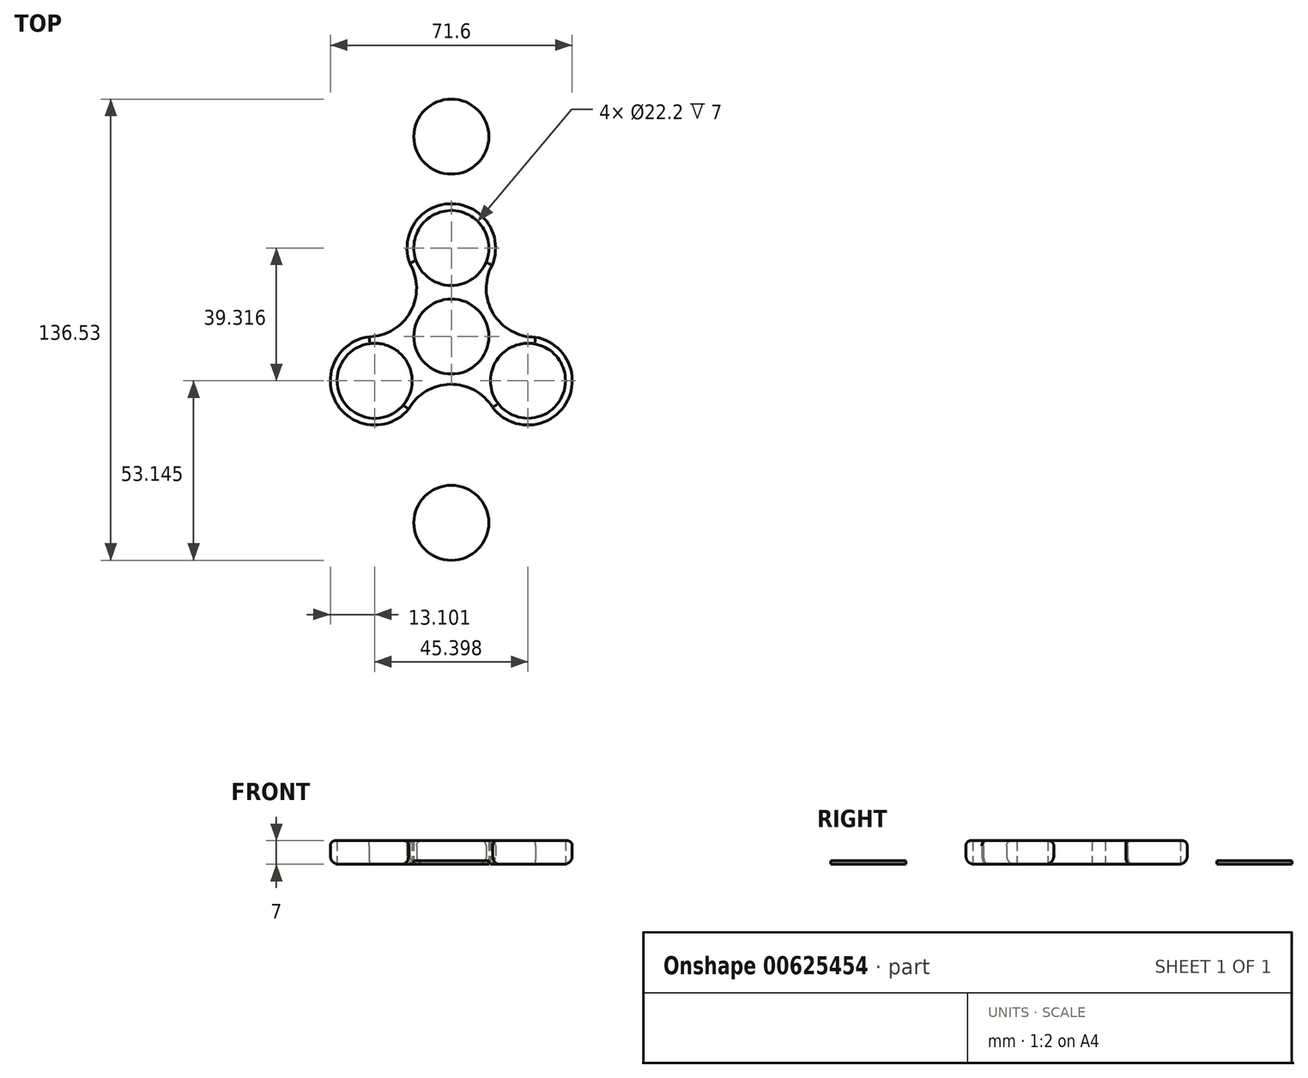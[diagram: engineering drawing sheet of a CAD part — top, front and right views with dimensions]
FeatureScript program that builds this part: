
annotation { "Feature Type Name" : "Feature", "Feature Type Description" : "" }
export const myFeature = defineFeature(function(context is Context, id is Id, definition is map)
    precondition{}
    {
        {
            var Q0;
            Q0=qCreatedBy(makeId("Top.planeOp"),FACE);
            var sketch = newSketch(context, id + "F0", { "sketchPlane" : qUnion([Q0])});
            skCircle(sketch, "E0", {"center": v(0, 0) * mm, "radius": 11.1 * mm});
            skCircle(sketch, "E1", {"center": v(0, 26.21) * mm, "radius": 11.1 * mm});
            skCircle(sketch, "E2.1.0", {"center": v(-22.7, -13.1) * mm, "radius": 11.1 * mm});
            skCircle(sketch, "E2.2.0", {"center": v(22.7, -13.1) * mm, "radius": 11.1 * mm});
            skArc(sketch, "E2.2.1", {"start": v(12.11, -20.82) * mm, "mid": v(33.83, -20.01) * mm, "end": v(24.9, -0.2) * mm});
            skArc(sketch, "E3", {"start": v(-24.31, -0.1) * mm, "mid": v(-34.06, -19.62) * mm, "end": v(-12.3, -21.06) * mm});
            skArc(sketch, "E4", {"start": v(-24.09, -0.08) * mm, "mid": v(-24.2, -0.1) * mm, "end": v(-24.31, -0.1) * mm});
            skArc(sketch, "E5", {"start": v(11.98, 20.9) * mm, "mid": v(12.02, 21) * mm, "end": v(12.06, 21.1) * mm});
            skArc(sketch, "E6", {"start": v(12.06, 21.1) * mm, "mid": v(0.2, 39.3) * mm, "end": v(-12.21, 21.47) * mm});
            skArc(sketch, "E7", {"start": v(12.06, 21.1) * mm, "mid": v(12.41, 6.8) * mm, "end": v(24.9, -0.2) * mm});
            skArc(sketch, "E8.1.0", {"start": v(-24.31, -0.1) * mm, "mid": v(-12.1, 7.35) * mm, "end": v(-12.29, 21.67) * mm});
            skArc(sketch, "E8.2.0", {"start": v(12.25, -21) * mm, "mid": v(-0.32, -14.15) * mm, "end": v(-12.62, -21.48) * mm});
            skPoint(sketch, "E9.start.orphan", {"position": v(0, 24.31) * mm});
            skSolve(sketch);
        }
        {
            var Q0;
            Q0=makeQuery(id+"F0.imprint","IMPRINT",FACE,{"disambiguationData":[TD([[makeQuery(id+"F0.imprint","IMPRINT",EDGE,{"derivedFrom":sQuery(id+"F0.wireOp",EDGE,"E0")}),-1.0]])]});
            extrude(context, id + "F1", {"entities" : qUnion([Q0]), "depth" : 7 * mm, "offsetDistance" : 25 * mm});
        }
        {
            var Q0;
            Q0=makeQuery(id+"F1.opExtrude","CAP_EDGE",EDGE,{"disambiguationData":[OSD([sQuery(id+"F0.wireOp",EDGE,"E8.2.0")])],"isStart":false});
            var Q1;
            Q1=makeQuery(id+"F1.opExtrude","CAP_EDGE",EDGE,{"disambiguationData":[OSD([sQuery(id+"F0.wireOp",EDGE,"E3")])],"isStart":false});
            var Q2;
            Q2=makeQuery(id+"F1.opExtrude","CAP_EDGE",EDGE,{"disambiguationData":[OSD([sQuery(id+"F0.wireOp",EDGE,"E8.1.0")])],"isStart":false});
            var Q3;
            Q3=makeQuery(id+"F1.opExtrude","CAP_EDGE",EDGE,{"disambiguationData":[OSD([sQuery(id+"F0.wireOp",EDGE,"E7")])],"isStart":false});
            var Q4;
            Q4=makeQuery(id+"F1.opExtrude","CAP_EDGE",EDGE,{"disambiguationData":[OSD([sQuery(id+"F0.wireOp",EDGE,"E6")])],"isStart":false});
            var Q5;
            Q5=makeQuery(id+"F1.opExtrude","CAP_EDGE",EDGE,{"disambiguationData":[OSD([sQuery(id+"F0.wireOp",EDGE,"E2.2.1")])],"isStart":false});
            fillet(context, id + "F2", {"entities" : qUnion([Q0, Q1, Q2, Q3, Q4, Q5]), "radius" : 1.5 * mm, "tangentPropagation" : true, "allowEdgeOverflow" : false});
        }
        {
            var Q0;
            Q0=makeQuery(id+"F1.opExtrude","CAP_EDGE",EDGE,{"disambiguationData":[OSD([sQuery(id+"F0.wireOp",EDGE,"E8.2.0")])],"isStart":true});
            var Q1;
            Q1=makeQuery(id+"F1.opExtrude","CAP_EDGE",EDGE,{"disambiguationData":[OSD([sQuery(id+"F0.wireOp",EDGE,"E3")])],"isStart":true});
            var Q2;
            Q2=makeQuery(id+"F1.opExtrude","CAP_EDGE",EDGE,{"disambiguationData":[OSD([sQuery(id+"F0.wireOp",EDGE,"E2.2.1")])],"isStart":true});
            var Q3;
            Q3=makeQuery(id+"F1.opExtrude","CAP_EDGE",EDGE,{"disambiguationData":[OSD([sQuery(id+"F0.wireOp",EDGE,"E7")])],"isStart":true});
            var Q4;
            Q4=makeQuery(id+"F1.opExtrude","CAP_EDGE",EDGE,{"disambiguationData":[OSD([sQuery(id+"F0.wireOp",EDGE,"E6")])],"isStart":true});
            var Q5;
            Q5=makeQuery(id+"F1.opExtrude","CAP_EDGE",EDGE,{"disambiguationData":[OSD([sQuery(id+"F0.wireOp",EDGE,"E8.1.0")])],"isStart":true});
            fillet(context, id + "F3", {"entities" : qUnion([Q0, Q1, Q2, Q3, Q4, Q5]), "radius" : 2.5 * mm, "tangentPropagation" : true, "allowEdgeOverflow" : false});
        }
        {
            var Q0;
            Q0=qCreatedBy(makeId("Top.planeOp"),FACE);
            var sketch = newSketch(context, id + "F4", { "sketchPlane" : qUnion([Q0])});
            skCircle(sketch, "E10", {"center": v(0, -55.15) * mm, "radius": 11.1 * mm});
            skCircle(sketch, "E11", {"center": v(0, 59.18) * mm, "radius": 11.1 * mm});
            skArc(sketch, "E12", {"start": v(-1.77, -50.53) * mm, "mid": v(-4.95, -55.24) * mm, "end": v(-1.6, -59.83) * mm});
            skArc(sketch, "E13", {"start": v(1.63, -59.82) * mm, "mid": v(4.95, -55.25) * mm, "end": v(1.83, -50.55) * mm});
            skArc(sketch, "E14", {"start": v(-2.36, 63.53) * mm, "mid": v(-4.95, 59) * mm, "end": v(-2.05, 54.68) * mm});
            skArc(sketch, "E15", {"start": v(2.1, 54.7) * mm, "mid": v(4.95, 59.2) * mm, "end": v(2.07, 63.68) * mm});
            skSolve(sketch);
        }
        {
            var Q0;
            Q0=makeQuery(id+"F4.imprint","IMPRINT",FACE,{"disambiguationData":[TD([[makeQuery(id+"F4.imprint","IMPRINT",EDGE,{"derivedFrom":sQuery(id+"F4.wireOp",EDGE,"E10")}),1.0]])]});
            extrude(context, id + "F5", {"entities" : qUnion([Q0]), "depth" : 1 * mm, "offsetDistance" : 25 * mm});
        }
        {
            var Q0;
            Q0=makeQuery(id+"F4.imprint","IMPRINT",FACE,{"disambiguationData":[TD([[makeQuery(id+"F4.imprint","IMPRINT",EDGE,{"derivedFrom":sQuery(id+"F4.wireOp",EDGE,"E11")}),1.0]])]});
            extrude(context, id + "F6", {"entities" : qUnion([Q0]), "depth" : 1 * mm, "offsetDistance" : 25 * mm});
        }
        {
            var Q0;
            Q0=sQuery(id+"F4.wireOp",EDGE,"E15");
            extrude(context, id + "F7", {"bodyType" : ToolBodyType.SURFACE, "surfaceEntities" : qUnion([Q0]), "depth" : 3 * mm, "offsetDistance" : 25 * mm});
        }
        {
            var Q0;
            Q0=sQuery(id+"F4.wireOp",EDGE,"E14");
            extrude(context, id + "F8", {"bodyType" : ToolBodyType.SURFACE, "surfaceEntities" : qUnion([Q0]), "depth" : 3 * mm, "offsetDistance" : 25 * mm});
        }
        {
            var Q0;
            Q0=sQuery(id+"F4.wireOp",EDGE,"E12");
            extrude(context, id + "F9", {"bodyType" : ToolBodyType.SURFACE, "surfaceEntities" : qUnion([Q0]), "depth" : 3 * mm, "offsetDistance" : 25 * mm});
        }
        {
            var Q0;
            Q0=sQuery(id+"F4.wireOp",EDGE,"E13");
            extrude(context, id + "F10", {"bodyType" : ToolBodyType.SURFACE, "surfaceEntities" : qUnion([Q0]), "depth" : 3 * mm, "offsetDistance" : 25 * mm});
        }
    });
